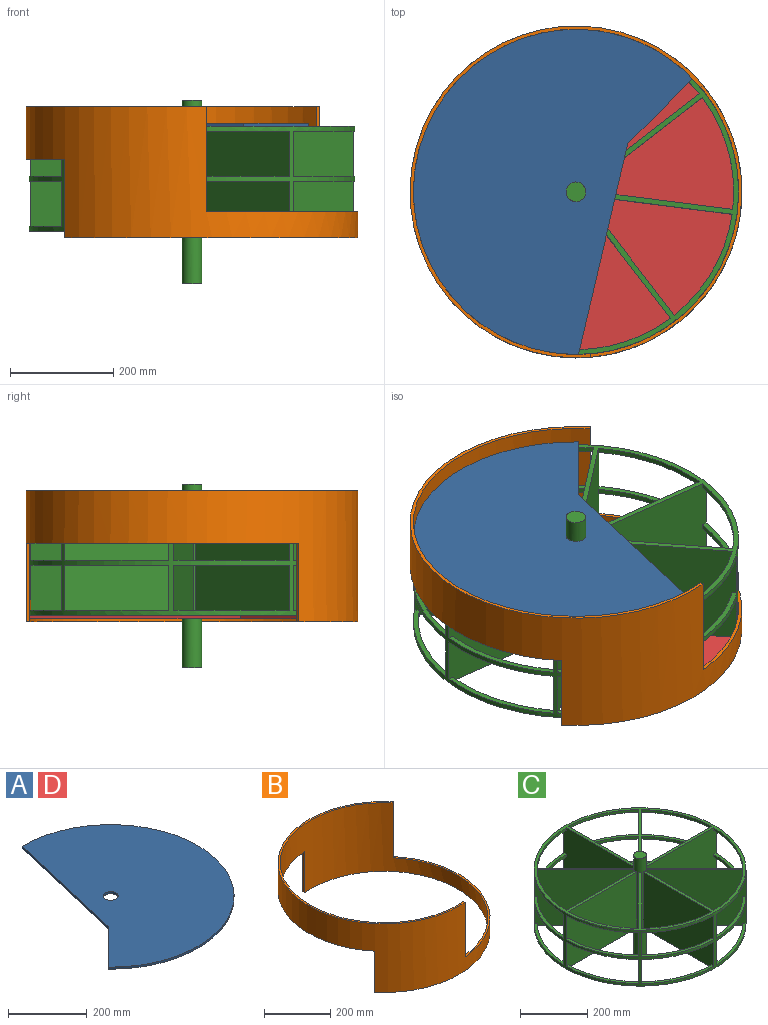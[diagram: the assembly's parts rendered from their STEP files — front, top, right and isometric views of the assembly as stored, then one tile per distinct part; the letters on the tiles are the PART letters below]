
ASSEMBLY  parts=4 mates=3
PART A: 6 faces, bbox 539.9x628.7x6.4 mm
  f0: plane 407.64x95.32mm, normal (-0.97,0.23,0), area 2658.3mm2, adj f1,f3,f4,f5
  f1: plane 125.52x125.52mm, normal (-0.71,0.71,0), area 1127.2mm2, adj f0,f3,f4,f5
  f2: cylinder r=19.05mm len=38.1mm, axis (0,0,-1), area 760.1mm2, adj f4,f5
  f3: cylinder r=314.33mm len=628.65mm, axis (0,0,-1), area 7898.6mm2, adj f0,f1,f4,f5
  f4: plane 628.65x539.93mm, normal (0,0,1), area 210723.4mm2, adj f0,f1,f2,f3
  f5: plane 628.65x539.93mm, normal (0,0,-1), area 210723.4mm2, adj f0,f1,f2,f3
PART B: 10 faces, bbox 641.4x641.4x254 mm
  f0: cylinder r=314.33mm len=628.65mm, axis (0,0,-1), area 257787.4mm2, adj f1,f2,f4,f5,f6,f7,f8,f9
  f1: plane 641.35x566.33mm, normal (0,0,-1), area 8269.2mm2, adj f0,f3,f7,f8
  f2: plane 641.35x566.33mm, normal (0,0,1), area 8269.2mm2, adj f0,f3,f4,f5
  f3: cylinder r=320.68mm len=641.35mm, axis (0,0,-1), area 262995.3mm2, adj f1,f2,f4,f5,f6,f7,f8,f9
  f4: plane 203.2x4.86mm, normal (0.64,-0.77,0), area 1290.3mm2, adj f0,f2,f3,f6
  f5: plane 203.2x6.33mm, normal (1,0.09,0), area 1290.3mm2, adj f0,f2,f3,f6
  f6: plane 525.58x293.28mm, normal (0,0,1), area 4398.5mm2, adj f0,f3,f4,f5
  f7: plane 152.4x6.33mm, normal (-1,-0.09,0), area 967.7mm2, adj f0,f1,f3,f9
  f8: plane 152.4x4.86mm, normal (-0.64,0.77,0), area 967.7mm2, adj f0,f1,f3,f9
  f9: plane 525.58x293.28mm, normal (0,0,-1), area 4398.5mm2, adj f0,f3,f7,f8
PART C: 78 faces, bbox 628.7x628.7x355.6 mm
  f0: plane 214.11x95.42mm, normal (0,0,1), area 2225.1mm2, adj f1,f53,f54,f76
  f1: cylinder r=304.8mm len=207.37mm, axis (0,0,-1), area 2189.5mm2, adj f0,f54,f56,f76
  f2: cylinder r=304.8mm len=207.37mm, axis (0,0,-1), area 2189.5mm2, adj f3,f4,f54,f76
  f3: plane 214.11x95.42mm, normal (0,0,1), area 2225.1mm2, adj f2,f53,f54,f76
  f4: plane 214.11x95.42mm, normal (0,0,-1), area 2225.1mm2, adj f2,f53,f54,f76
  f5: plane 214.11x95.42mm, normal (0,0,-1), area 2225.1mm2, adj f6,f53,f54,f76
  f6: cylinder r=304.8mm len=207.37mm, axis (0,0,-1), area 2189.5mm2, adj f5,f54,f55,f76
  f7: plane 214.11x95.42mm, normal (0,0,1), area 2225.1mm2, adj f8,f53,f74,f77
  f8: cylinder r=304.8mm len=207.37mm, axis (0,0,-1), area 2189.5mm2, adj f7,f56,f74,f77
  f9: cylinder r=304.8mm len=207.37mm, axis (0,0,-1), area 2189.5mm2, adj f10,f11,f74,f77
  f10: plane 214.11x95.42mm, normal (0,0,1), area 2225.1mm2, adj f9,f53,f74,f77
  f11: plane 214.11x95.42mm, normal (0,0,-1), area 2225.1mm2, adj f9,f53,f74,f77
  f12: plane 214.11x95.42mm, normal (0,0,-1), area 2225.1mm2, adj f13,f53,f74,f77
  f13: cylinder r=304.8mm len=207.37mm, axis (0,0,-1), area 2189.5mm2, adj f12,f55,f74,f77
  f14: plane 214.11x95.42mm, normal (0,0,1), area 2225.1mm2, adj f15,f53,f72,f75
  f15: cylinder r=304.8mm len=207.37mm, axis (0,0,-1), area 2189.5mm2, adj f14,f56,f72,f75
  f16: cylinder r=304.8mm len=207.37mm, axis (0,0,-1), area 2189.5mm2, adj f17,f18,f72,f75
  f17: plane 214.11x95.42mm, normal (0,0,1), area 2225.1mm2, adj f16,f53,f72,f75
  f18: plane 214.11x95.42mm, normal (0,0,-1), area 2225.1mm2, adj f16,f53,f72,f75
  f19: plane 214.11x95.42mm, normal (0,0,-1), area 2225.1mm2, adj f20,f53,f72,f75
  f20: cylinder r=304.8mm len=207.37mm, axis (0,0,-1), area 2189.5mm2, adj f19,f55,f72,f75
  f21: plane 214.11x95.42mm, normal (0,0,1), area 2225.1mm2, adj f22,f53,f70,f73
  f22: cylinder r=304.8mm len=207.37mm, axis (0,0,-1), area 2189.5mm2, adj f21,f56,f70,f73
  f23: cylinder r=304.8mm len=207.37mm, axis (0,0,-1), area 2189.5mm2, adj f24,f25,f70,f73
  f24: plane 214.11x95.42mm, normal (0,0,1), area 2225.1mm2, adj f23,f53,f70,f73
  f25: plane 214.11x95.42mm, normal (0,0,-1), area 2225.1mm2, adj f23,f53,f70,f73
  f26: plane 214.11x95.42mm, normal (0,0,-1), area 2225.1mm2, adj f27,f53,f70,f73
  f27: cylinder r=304.8mm len=207.37mm, axis (0,0,-1), area 2189.5mm2, adj f26,f55,f70,f73
  f28: plane 214.11x95.42mm, normal (0,0,1), area 2225.1mm2, adj f29,f53,f68,f71
  f29: cylinder r=304.8mm len=207.37mm, axis (0,0,-1), area 2189.5mm2, adj f28,f56,f68,f71
  f30: cylinder r=304.8mm len=207.37mm, axis (0,0,-1), area 2189.5mm2, adj f31,f32,f68,f71
  f31: plane 214.11x95.42mm, normal (0,0,1), area 2225.1mm2, adj f30,f53,f68,f71
  f32: plane 214.11x95.42mm, normal (0,0,-1), area 2225.1mm2, adj f30,f53,f68,f71
  f33: plane 214.11x95.42mm, normal (0,0,-1), area 2225.1mm2, adj f34,f53,f68,f71
  f34: cylinder r=304.8mm len=207.37mm, axis (0,0,-1), area 2189.5mm2, adj f33,f55,f68,f71
  f35: plane 214.11x95.42mm, normal (0,0,1), area 2225.1mm2, adj f36,f53,f66,f69
  f36: cylinder r=304.8mm len=207.37mm, axis (0,0,-1), area 2189.5mm2, adj f35,f56,f66,f69
  f37: cylinder r=304.8mm len=207.37mm, axis (0,0,-1), area 2189.5mm2, adj f38,f39,f66,f69
  f38: plane 214.11x95.42mm, normal (0,0,1), area 2225.1mm2, adj f37,f53,f66,f69
  f39: plane 214.11x95.42mm, normal (0,0,-1), area 2225.1mm2, adj f37,f53,f66,f69
  f40: plane 214.11x95.42mm, normal (0,0,-1), area 2225.1mm2, adj f41,f53,f66,f69
  f41: cylinder r=304.8mm len=207.37mm, axis (0,0,-1), area 2189.5mm2, adj f40,f55,f66,f69
  f42: plane 214.11x95.42mm, normal (0,0,1), area 2225.1mm2, adj f43,f53,f64,f67
  f43: cylinder r=304.8mm len=207.37mm, axis (0,0,-1), area 2189.5mm2, adj f42,f56,f64,f67
  f44: cylinder r=304.8mm len=207.37mm, axis (0,0,-1), area 2189.5mm2, adj f45,f46,f64,f67
  f45: plane 214.11x95.42mm, normal (0,0,1), area 2225.1mm2, adj f44,f53,f64,f67
  f46: plane 214.11x95.42mm, normal (0,0,-1), area 2225.1mm2, adj f44,f53,f64,f67
  f47: plane 214.11x95.42mm, normal (0,0,-1), area 2225.1mm2, adj f48,f53,f64,f67
  f48: cylinder r=304.8mm len=207.37mm, axis (0,0,-1), area 2189.5mm2, adj f47,f55,f64,f67
  f49: cylinder r=19.05mm len=355.6mm, axis (0,0,-1), area 26913.6mm2, adj f50,f51,f52,f54,f55,f56,f64,f65
  f50: plane 38.1x38.1mm, normal (0,0,1), area 1140.1mm2, adj f49
  f51: plane 38.1x38.1mm, normal (0,0,-1), area 1140.1mm2, adj f49
  f52: plane 295.84x203.2mm, normal (1,0,0), area 59843.3mm2, adj f49,f53,f55,f56,f57,f58,f59,f60
  f53: cylinder r=314.33mm len=628.65mm, axis (0,0,-1), area 69741.5mm2, adj f0,f3,f4,f5,f7,f10,f11,f12
  f54: plane 295.84x203.2mm, normal (-1,0,0), area 59843.3mm2, adj f0,f1,f2,f3,f4,f5,f6,f49
  f55: plane 628.65x628.65mm, normal (0,0,1), area 40315mm2, adj f6,f13,f20,f27,f34,f41,f48,f49
  f56: plane 628.65x628.65mm, normal (0,0,-1), area 40315mm2, adj f1,f8,f15,f22,f29,f36,f43,f49
  f57: plane 214.11x95.42mm, normal (0,0,1), area 2225.1mm2, adj f52,f53,f58,f65
  f58: cylinder r=304.8mm len=207.37mm, axis (0,0,-1), area 2189.5mm2, adj f52,f56,f57,f65
  f59: cylinder r=304.8mm len=207.37mm, axis (0,0,-1), area 2189.5mm2, adj f52,f60,f61,f65
  f60: plane 214.11x95.42mm, normal (0,0,1), area 2225.1mm2, adj f52,f53,f59,f65
  f61: plane 214.11x95.42mm, normal (0,0,-1), area 2225.1mm2, adj f52,f53,f59,f65
  f62: plane 214.11x95.42mm, normal (0,0,-1), area 2225.1mm2, adj f52,f53,f63,f65
  f63: cylinder r=304.8mm len=207.37mm, axis (0,0,-1), area 2189.5mm2, adj f52,f55,f62,f65
  f64: plane 209.19x209.19mm, normal (0.71,-0.71,0), area 59843.3mm2, adj f42,f43,f44,f45,f46,f47,f48,f49
  f65: plane 209.19x209.19mm, normal (-0.71,0.71,0), area 59843.3mm2, adj f49,f53,f55,f56,f57,f58,f59,f60
  f66: plane 295.84x203.2mm, normal (0,-1,0), area 59843.3mm2, adj f35,f36,f37,f38,f39,f40,f41,f49
  f67: plane 295.84x203.2mm, normal (0,1,0), area 59843.3mm2, adj f42,f43,f44,f45,f46,f47,f48,f49
  f68: plane 209.19x209.19mm, normal (-0.71,-0.71,0), area 59843.3mm2, adj f28,f29,f30,f31,f32,f33,f34,f49
  f69: plane 209.19x209.19mm, normal (0.71,0.71,0), area 59843.3mm2, adj f35,f36,f37,f38,f39,f40,f41,f49
  f70: plane 295.84x203.2mm, normal (-1,0,0), area 59843.3mm2, adj f21,f22,f23,f24,f25,f26,f27,f49
  f71: plane 295.84x203.2mm, normal (1,0,0), area 59843.3mm2, adj f28,f29,f30,f31,f32,f33,f34,f49
  f72: plane 209.19x209.19mm, normal (-0.71,0.71,0), area 59843.3mm2, adj f14,f15,f16,f17,f18,f19,f20,f49
  f73: plane 209.19x209.19mm, normal (0.71,-0.71,0), area 59843.3mm2, adj f21,f22,f23,f24,f25,f26,f27,f49
  f74: plane 295.84x203.2mm, normal (0,1,0), area 59843.3mm2, adj f7,f8,f9,f10,f11,f12,f13,f49
  f75: plane 295.84x203.2mm, normal (0,-1,0), area 59843.3mm2, adj f14,f15,f16,f17,f18,f19,f20,f49
  f76: plane 209.19x209.19mm, normal (0.71,0.71,0), area 59843.3mm2, adj f0,f1,f2,f3,f4,f5,f6,f49
  f77: plane 209.19x209.19mm, normal (-0.71,-0.71,0), area 59843.3mm2, adj f7,f8,f9,f10,f11,f12,f13,f49
PART D: same geometry as A
PLACE A rot(axis=(0,0,1),180deg) t=(-609.6,0,215.9)mm
PLACE B at identity fixed
PLACE C rot(axis=(0,0,1),127.7deg) t=(-491.38,241.02,215.9)mm
PLACE D t=(0,0,6.35)mm
MATE fastened A.f2 <-> D.f2  axis (0,0,-1) through (-304.8,0,419.1)mm
MATE revolute C.f1 <-> D.f2  axis (0,0,-1) through (-304.8,0,215.9)mm
MATE fastened B.f0 <-> D.f2  axis (0,0,-1) through (-304.8,0,203.2)mm
